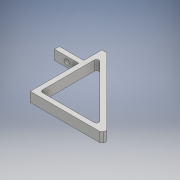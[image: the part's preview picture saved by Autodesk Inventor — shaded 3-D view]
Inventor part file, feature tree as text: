
AUTODESK INVENTOR PART (.ipt)
format: ipt  version: 2018 (Build 220112000, 112)  size: 154,112 bytes
history: native  units: mm
features: extrude x4, sketch x4, fillet x1, projected_geometry x1
ambient origin geometry x8: Origin, YZ Plane, XZ Plane, XY Plane, X Axis, Y Axis, Z Axis, Center Point
bodies: Solid1 (feature_tree)
feature tree (10):
  extrude  "Extrusion1"  Depth=8.0mm TaperAngle=0.0deg
  extrude  "Extrusion4"  Depth=4.0mm
  extrude  "Extrusion5"  Depth=4.0mm
  extrude  "Extrusion6"  Depth=2.0mm
  fillet  "Fillet1"  Radius=4.0mm
  sketch  "Sketch1"  dims[d0=4.0mm d6=8.0mm d7=0.0mm]
  sketch  "Sketch5"  dims[d19=4.0mm d21=4.0mm]
  projected_geometry  "Projected Loop1"
  sketch  "Sketch6"  dims[d22=20.0mm d23=4.0mm]
  sketch  "Sketch7"  dims[d25=45.0deg d28=83.4386mm d29=4.0mm d30=4.0mm d31=4.2mm d32=10.0mm d33=6.0mm d34=0.0mm d35=40.0mm d36=49.5mm d37=20.0mm d38=3.2mm d39=6.0mm d40=0.0mm d42=4.0mm d43=6.0mm d44=0.0mm d45=2.0mm]
